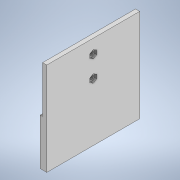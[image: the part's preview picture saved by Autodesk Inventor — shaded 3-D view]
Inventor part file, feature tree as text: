
AUTODESK INVENTOR PART (.ipt)
format: ipt  version: 2021 (Build 250183000, 183)  size: 135,168 bytes
history: native  units: mm
features: sketch x4, extrude x3, projected_geometry x2, hole x1
ambient origin geometry x8: Origin, YZ Plane, XZ Plane, XY Plane, X Axis, Y Axis, Z Axis, Center Point
bodies: Solid1 (feature_tree)
feature tree (10):
  extrude  "Extrusion1"  Depth=100.0mm
  extrude  "Extrusion2"  Depth=2.5mm TaperAngle=0.0deg
  hole  "Hole1"  [1 undecoded]
  extrude  "Extrusion3"  Depth=7.5mm
  sketch  "Sketch1"  dims[d0=100.0mm d1=100.0mm]
  sketch  "Sketch2"  dims[d2=4.5mm d3=0.0mm d4=2.5mm d5=0.0mm]
  sketch  "Sketch3"  dims[d6=37.5mm d7=15.0mm]
  projected_geometry  "Projected Loop1"
  sketch  "Sketch4"  dims[d8=4.5mm d9=6.0mm d10=4.0mm d11=2.0mm d12=90.0deg d13=8.0mm d14=20.594885mm d15=7.5mm d16=7.5mm d17=2.25mm d18=0.0mm]
  projected_geometry  "Projected Loop2"
note: 1 required parameter value undecoded (feature->parameter linkage not recoverable at this tier; creation-order binding heuristic only, values carry confidence <= 0.55)
